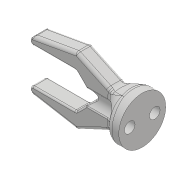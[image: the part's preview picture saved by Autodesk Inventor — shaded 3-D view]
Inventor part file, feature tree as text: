
AUTODESK INVENTOR PART (.ipt)
format: ipt  version: 2018 (Build 220112000, 112)  size: 963,072 bytes
history: native  units: mm
features: fillet x8, sketch x7, projected_geometry x5, extrude x4, plane x3, mirror x1, loft x1, hole x1, other x1
ambient origin geometry x8: Origin, YZ Plane, XZ Plane, XY Plane, X Axis, Y Axis, Z Axis, Center Point
bodies: Solid1 (feature_tree)
feature tree (31):
  extrude  "Extrusion1"  TaperAngle=60.0deg  [1 undecoded]
  mirror  "Mirror1"
  plane  "Work Plane1"
  sketch  "Sketch2"  dims[d2=25.307274mm d3=25.307274mm]
  plane  "Work Plane2"
  extrude  "Extrusion2"  Depth=25.307274mm
  loft  "Loft1"
  extrude  "Extrusion3"  Depth=7.0mm
  fillet  "Fillet1"  Radius=11.0mm
  fillet  "Fillet2"  Radius=14.0mm
  fillet  "Fillet3"  Radius=16.0mm
  fillet  "Fillet4"  Radius=5.0mm
  fillet  "Fillet5"  Radius=10.0mm
  fillet  "Fillet6"  [1 undecoded]
  hole  "Hole1"  [1 undecoded]
  plane  "Work Plane3"
  extrude  "Extrusion4"  TaperAngle=0.0deg  [1 undecoded]
  fillet  "Fillet7"  Radius=3.0mm
  fillet  "Fillet8"  Radius=2.0mm
  sketch  "Sketch1"  dims[d0=8.0mm d1=60.0deg]
  sketch  "Sketch3"  dims[d4=135.0deg d5=135.0deg]
  sketch  "Sketch4"  dims[d6=8.0mm d7=7.0mm d8=11.0mm d9=14.0mm d10=16.0mm d11=5.0mm d12=0.0mm d13=10.0mm d14=-5.0mm]
  projected_geometry  "Projected Loop1"
  other  "Edges1"
  sketch  "Sketch5"  dims[d15=5.0mm d16=0.0mm d17=15.0mm]
  projected_geometry  "Projected Loop2"
  sketch  "Sketch6"  dims[d18=0.0mm d19=90.0deg d20=0.0mm d21=90.0deg d22=3.0mm d23=0.0mm d24=2.0mm]
  projected_geometry  "Projected Loop3"
  sketch  "Sketch7"  dims[d25=2.0mm d26=2.0mm d27=1.0mm d28=1.0mm d29=0.5mm d30=8.0mm d31=3.4mm d32=6.0mm d33=6.3mm d34=2.0mm d35=90.0deg d36=8.0mm d37=20.594885mm d38=-5.0mm d39=6.0mm d40=6.0mm d41=14.0mm d42=0.0mm d43=0.5mm d44=0.1mm]
  projected_geometry  "Projected Loop4"
  projected_geometry  "Project Cut Edges1"
note: 4 required parameter values undecoded (feature->parameter linkage not recoverable at this tier; creation-order binding heuristic only, values carry confidence <= 0.55)
